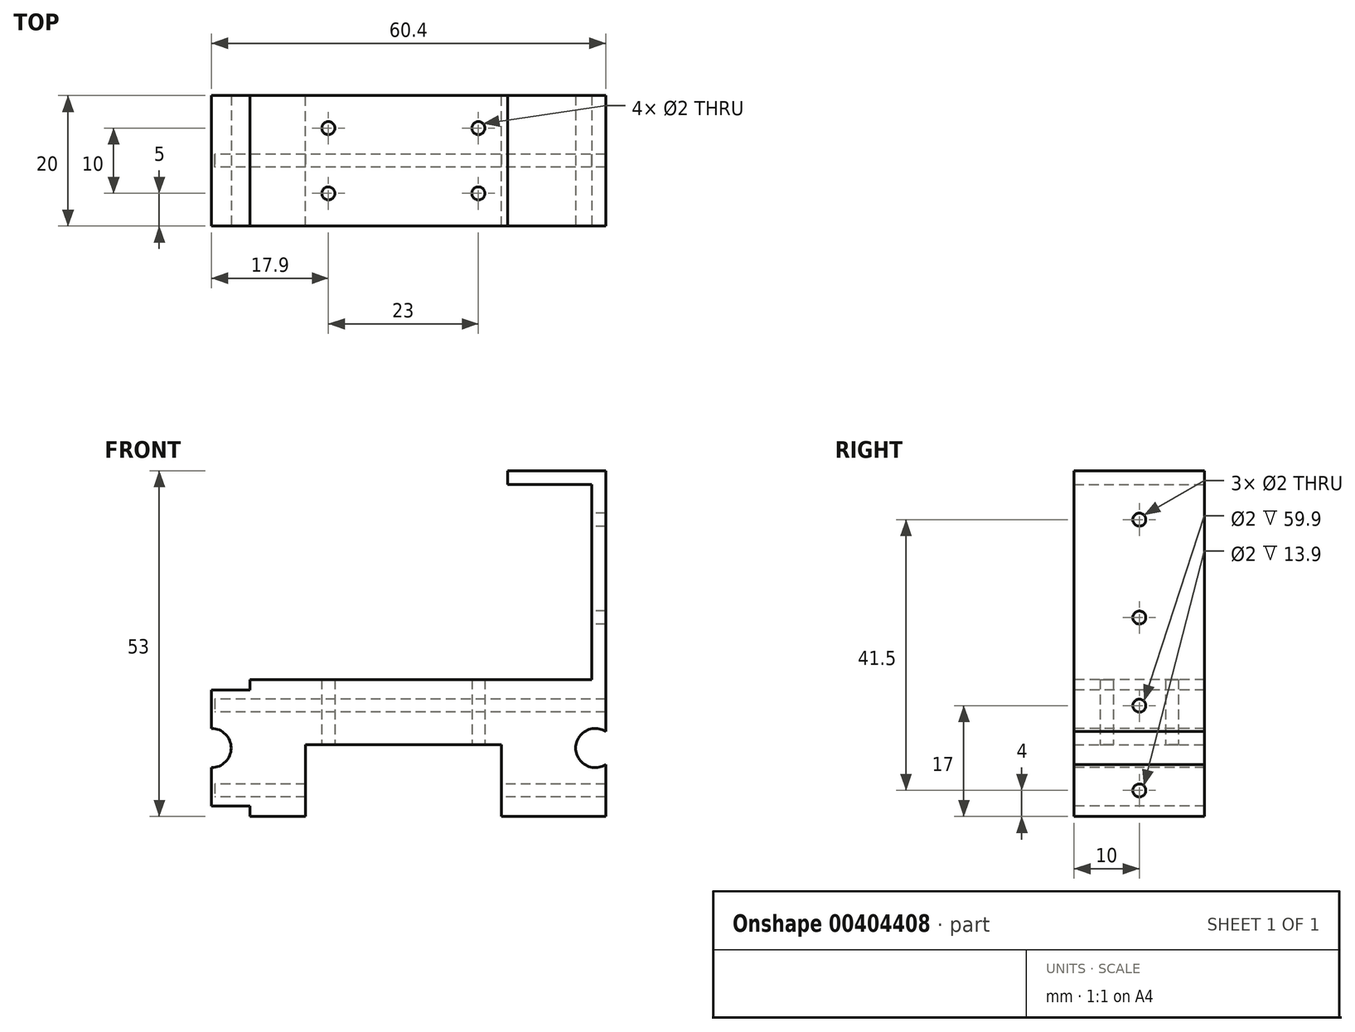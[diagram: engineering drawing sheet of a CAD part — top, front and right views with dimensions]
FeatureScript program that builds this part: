
annotation { "Feature Type Name" : "Feature", "Feature Type Description" : "" }
export const myFeature = defineFeature(function(context is Context, id is Id, definition is map)
    precondition{}
    {
        {
            var Q0;
            Q0=qCreatedBy(makeId("Front.planeOp"),FACE);
            var sketch = newSketch(context, id + "F0", { "sketchPlane" : qUnion([Q0])});
            skLineSegment(sketch, "E0.bottom", {"start": v(31, 26.5) * mm, "end": v(-31, 26.5) * mm});
            skLineSegment(sketch, "E0.top", {"start": v(31, -26.5) * mm, "end": v(-31, -26.5) * mm});
            skLineSegment(sketch, "E0.left", {"start": v(31, 26.5) * mm, "end": v(31, -26.5) * mm});
            skLineSegment(sketch, "E0.right", {"start": v(-31, 26.5) * mm, "end": v(-31, -26.5) * mm});
            skPoint(sketch, "E0.middle", {"position": v(0, 0) * mm});
            skSolve(sketch);
        }
        {
            var Q0;
            Q0=makeQuery(id+"F0.imprint","IMPRINT",FACE,{"disambiguationData":[TD([[makeQuery(id+"F0.imprint","IMPRINT",EDGE,{"derivedFrom":sQuery(id+"F0.wireOp",EDGE,"E0.bottom")}),1.0]])]});
            extrude(context, id + "F1", {"entities" : qUnion([Q0]), "endBound" : BoundingType.SYMMETRIC, "depth" : 20 * mm});
        }
        {
            var Q0;
            Q0=makeQuery(id+"F1.opExtrude","CAP_FACE",FACE,{"disambiguationData":[OSD([sQuery(id+"F0.wireOp",EDGE,"E0.bottom"),sQuery(id+"F0.wireOp",EDGE,"E0.top"),sQuery(id+"F0.wireOp",EDGE,"E0.left"),sQuery(id+"F0.wireOp",EDGE,"E0.right")])],"isStart":false});
            var sketch = newSketch(context, id + "F2", { "sketchPlane" : qUnion([Q0])});
            skLineSegment(sketch, "E1", {"start": v(-31, 26.5) * mm, "end": v(-31, -5.5) * mm});
            skLineSegment(sketch, "E2", {"start": v(-31, -5.5) * mm, "end": v(-28.9, -5.5) * mm});
            skLineSegment(sketch, "E3", {"start": v(-28.9, -5.5) * mm, "end": v(-28.9, 24.4) * mm});
            skLineSegment(sketch, "E4", {"start": v(-28.9, 24.4) * mm, "end": v(-16, 24.4) * mm});
            skLineSegment(sketch, "E5", {"start": v(-16, 24.4) * mm, "end": v(-16, 26.5) * mm});
            skLineSegment(sketch, "E6", {"start": v(-16, 26.5) * mm, "end": v(-31, 26.5) * mm});
            skLineSegment(sketch, "E7", {"start": v(-23.5, -26.5) * mm, "end": v(-31, -26.5) * mm});
            skLineSegment(sketch, "E8", {"start": v(-31, -26.5) * mm, "end": v(-31, -5.5) * mm});
            skLineSegment(sketch, "E9", {"start": v(-31, -5.5) * mm, "end": v(-23.5, -5.5) * mm});
            skLineSegment(sketch, "E10", {"start": v(-23.5, -5.5) * mm, "end": v(-23.5, -7.1) * mm});
            skLineSegment(sketch, "E11", {"start": v(-23.5, -7.1) * mm, "end": v(-29.4, -7.1) * mm});
            skLineSegment(sketch, "E12", {"start": v(-29.4, -7.1) * mm, "end": v(-29.4, -24.9) * mm});
            skLineSegment(sketch, "E13", {"start": v(-29.4, -24.9) * mm, "end": v(-23.5, -24.9) * mm});
            skLineSegment(sketch, "E14", {"start": v(-23.5, -24.9) * mm, "end": v(-23.5, -26.5) * mm});
            skSolve(sketch);
        }
        {
            var Q0;
            {var subQ1=sQuery(id+"F2.wireOp",EDGE,"E1");Q0=makeQuery(id+"F2.imprint","IMPRINT",FACE,{"disambiguationData":[TD([[makeQuery(id+"F2.imprint","IMPRINT",EDGE,{"derivedFrom":subQ1}),1.0]])]});}
            var Q1;
            Q1=makeQuery(id+"F2.imprint","IMPRINT",FACE,{"disambiguationData":[TD([[makeQuery(id+"F2.imprint","IMPRINT",EDGE,{"derivedFrom":sQuery(id+"F2.wireOp",EDGE,"E7")}),-1.0]])]});
            extrude(context, id + "F3", {"entities" : qUnion([Q0, Q1]), "operationType" : NewBodyOperationType.REMOVE, "endBound" : BoundingType.UP_TO_NEXT, "oppositeDirection" : true, "depth" : 25 * mm});
        }
        {
            var Q0;
            Q0=makeQuery(id+"F3.boolean.opBoolean","COPY",FACE,{"derivedFrom":makeQuery(id+"F3.opExtrude","SWEPT_FACE",FACE,{"disambiguationData":[OSD([sQuery(id+"F2.wireOp",EDGE,"E3")])]})});
            var sketch = newSketch(context, id + "F4", { "sketchPlane" : qUnion([Q0])});
            skPoint(sketch, "E15", {"position": v(0, 19) * mm});
            skPoint(sketch, "E16", {"position": v(0, -9.5) * mm});
            skPoint(sketch, "E17", {"position": v(0, -22.5) * mm});
            skPoint(sketch, "E18", {"position": v(0, 4) * mm});
            skSolve(sketch);
        }
        {
            var Q0;
            Q0=sQuery(id+"F4.wireOp",VERTEX,"E15");
            var Q1;
            Q1=sQuery(id+"F4.wireOp",VERTEX,"E18");
            var Q2;
            Q2=sQuery(id+"F4.wireOp",VERTEX,"E16");
            var Q3;
            Q3=sQuery(id+"F4.wireOp",VERTEX,"E17");
            var Q4;
            Q4=makeQuery(id+"F1.opExtrude","SWEPT_BODY",BODY,{"disambiguationData":[OSD([sQuery(id+"F0.wireOp",EDGE,"E0.bottom"),sQuery(id+"F0.wireOp",EDGE,"E0.top"),sQuery(id+"F0.wireOp",EDGE,"E0.left"),sQuery(id+"F0.wireOp",EDGE,"E0.right")])]});
            hole(context, id + "F5", {"style" : HoleStyle.SIMPLE, "endStyle" : HoleEndStyle.THROUGH, "holeDiameter" : 2 * mm, "locations" : qUnion([Q0, Q1, Q2, Q3]), "scope" : qUnion([Q4]), "tappedDepth" : 12 * mm, "tapClearance" : 3});
        }
        {
            var Q0;
            Q0=makeQuery(id+"F1.opExtrude","CAP_FACE",FACE,{"disambiguationData":[OSD([sQuery(id+"F0.wireOp",EDGE,"E0.bottom"),sQuery(id+"F0.wireOp",EDGE,"E0.top"),sQuery(id+"F0.wireOp",EDGE,"E0.left"),sQuery(id+"F0.wireOp",EDGE,"E0.right")])],"isStart":false});
            var sketch = newSketch(context, id + "F6", { "sketchPlane" : qUnion([Q0])});
            skLineSegment(sketch, "E19.bottom", {"start": v(-7, 26.5) * mm, "end": v(2, 26.5) * mm});
            skLineSegment(sketch, "E19.top", {"start": v(-7, 22.25) * mm, "end": v(2, 22.25) * mm});
            skLineSegment(sketch, "E19.left", {"start": v(-7, 26.5) * mm, "end": v(-7, 22.25) * mm});
            skLineSegment(sketch, "E19.right", {"start": v(2, 26.5) * mm, "end": v(2, 22.25) * mm});
            skLineSegment(sketch, "E20.bottom", {"start": v(-7, 22.25) * mm, "end": v(-16, 22.25) * mm});
            skLineSegment(sketch, "E20.top", {"start": v(-7, 26.5) * mm, "end": v(-16, 26.5) * mm});
            skLineSegment(sketch, "E20.left", {"start": v(-7, 22.25) * mm, "end": v(-7, 26.5) * mm});
            skLineSegment(sketch, "E20.right", {"start": v(-16, 22.25) * mm, "end": v(-16, 26.5) * mm});
            skLineSegment(sketch, "E21.bottom", {"start": v(2, 22.25) * mm, "end": v(11, 22.25) * mm});
            skLineSegment(sketch, "E21.top", {"start": v(2, 26.5) * mm, "end": v(11, 26.5) * mm});
            skLineSegment(sketch, "E21.left", {"start": v(2, 22.25) * mm, "end": v(2, 26.5) * mm});
            skLineSegment(sketch, "E21.right", {"start": v(11, 22.25) * mm, "end": v(11, 26.5) * mm});
            skLineSegment(sketch, "E22.bottom", {"start": v(11, 22.25) * mm, "end": v(16, 22.25) * mm});
            skLineSegment(sketch, "E22.top", {"start": v(11, 26.5) * mm, "end": v(16, 26.5) * mm});
            skLineSegment(sketch, "E22.right", {"start": v(16, 22.25) * mm, "end": v(16, 26.5) * mm});
            skSolve(sketch);
        }
        {
            var Q0;
            Q0=makeQuery(id+"F6.imprint","IMPRINT",FACE,{"disambiguationData":[TD([[makeQuery(id+"F6.imprint","IMPRINT",EDGE,{"derivedFrom":sQuery(id+"F6.wireOp",EDGE,"E19.bottom")}),1.0]])]});
            var Q1;
            {var subQ2=sQuery(id+"F6.wireOp",EDGE,"E20.bottom");Q1=makeQuery(id+"F6.imprint","IMPRINT",FACE,{"disambiguationData":[TD([[makeQuery(id+"F6.imprint","IMPRINT",EDGE,{"derivedFrom":subQ2}),-1.0]])]});}
            var Q2;
            Q2=makeQuery(id+"F6.imprint","IMPRINT",FACE,{"disambiguationData":[TD([[makeQuery(id+"F6.imprint","IMPRINT",EDGE,{"derivedFrom":sQuery(id+"F6.wireOp",EDGE,"E21.bottom")}),1.0]])]});
            var Q3;
            {var subQ2=sQuery(id+"F6.wireOp",EDGE,"E22.bottom");Q3=makeQuery(id+"F6.imprint","IMPRINT",FACE,{"disambiguationData":[TD([[makeQuery(id+"F6.imprint","IMPRINT",EDGE,{"derivedFrom":subQ2}),1.0]])]});}
            extrude(context, id + "F7", {"entities" : qUnion([Q0, Q1, Q2, Q3]), "operationType" : NewBodyOperationType.REMOVE, "endBound" : BoundingType.UP_TO_NEXT, "oppositeDirection" : true, "depth" : 25 * mm});
        }
        {
            var Q0;
            Q0=makeQuery(id+"F1.opExtrude","CAP_FACE",FACE,{"disambiguationData":[OSD([sQuery(id+"F0.wireOp",EDGE,"E0.bottom"),sQuery(id+"F0.wireOp",EDGE,"E0.top"),sQuery(id+"F0.wireOp",EDGE,"E0.left"),sQuery(id+"F0.wireOp",EDGE,"E0.right")])],"isStart":false});
            var sketch = newSketch(context, id + "F8", { "sketchPlane" : qUnion([Q0])});
            skLineSegment(sketch, "E23.bottom", {"start": v(-28.9, -5.5) * mm, "end": v(28.9, -5.5) * mm});
            skLineSegment(sketch, "E23.top", {"start": v(-28.9, 24.4) * mm, "end": v(28.9, 24.4) * mm});
            skLineSegment(sketch, "E23.left", {"start": v(-28.9, -5.5) * mm, "end": v(-28.9, 24.4) * mm});
            skLineSegment(sketch, "E23.right", {"start": v(28.9, -5.5) * mm, "end": v(28.9, 24.4) * mm});
            skSolve(sketch);
        }
        {
            var Q0;
            Q0 = qSketchRegion(id + "F8", true);
            extrude(context, id + "F9", {"entities" : qUnion([Q0]), "operationType" : NewBodyOperationType.REMOVE, "oppositeDirection" : true, "depth" : 25 * mm});
        }
        {
            var Q0;
            Q0=makeQuery(id+"F1.opExtrude","SWEPT_FACE",FACE,{"disambiguationData":[OSD([sQuery(id+"F0.wireOp",EDGE,"E0.top")])]});
            var sketch = newSketch(context, id + "F10", { "sketchPlane" : qUnion([Q0])});
            skLineSegment(sketch, "E24.bottom", {"start": v(-15, 10) * mm, "end": v(15, 10) * mm});
            skLineSegment(sketch, "E24.top", {"start": v(-15, -10) * mm, "end": v(15, -10) * mm});
            skLineSegment(sketch, "E24.left", {"start": v(-15, 10) * mm, "end": v(-15, -10) * mm});
            skLineSegment(sketch, "E24.right", {"start": v(15, 10) * mm, "end": v(15, -10) * mm});
            skPoint(sketch, "E24.middle", {"position": v(0, 0) * mm});
            skSolve(sketch);
        }
        {
            var Q0;
            Q0 = qSketchRegion(id + "F10", true);
            extrude(context, id + "F11", {"entities" : qUnion([Q0]), "operationType" : NewBodyOperationType.REMOVE, "oppositeDirection" : true, "depth" : 11 * mm});
        }
        {
            var Q0;
            Q0=makeQuery(id+"F11.boolean.opBoolean","COPY",FACE,{"derivedFrom":makeQuery(id+"F11.opExtrude","CAP_FACE",FACE,{"disambiguationData":[OSD([sQuery(id+"F10.wireOp",EDGE,"E24.bottom"),sQuery(id+"F10.wireOp",EDGE,"E24.top"),sQuery(id+"F10.wireOp",EDGE,"E24.left"),sQuery(id+"F10.wireOp",EDGE,"E24.right")])],"isStart":false})});
            var sketch = newSketch(context, id + "F12", { "sketchPlane" : qUnion([Q0])});
            skLineSegment(sketch, "E25.bottom", {"start": v(-11.5, 5) * mm, "end": v(11.5, 5) * mm});
            skLineSegment(sketch, "E25.top", {"start": v(-11.5, -5) * mm, "end": v(11.5, -5) * mm});
            skLineSegment(sketch, "E25.left", {"start": v(-11.5, 5) * mm, "end": v(-11.5, -5) * mm});
            skLineSegment(sketch, "E25.right", {"start": v(11.5, 5) * mm, "end": v(11.5, -5) * mm});
            skPoint(sketch, "E25.middle", {"position": v(0, 0) * mm});
            skSolve(sketch);
        }
        {
            var Q0;
            Q0=sQuery(id+"F12.wireOp",VERTEX,"E25.bottom.start");
            var Q1;
            Q1=sQuery(id+"F12.wireOp",VERTEX,"E25.right.start");
            var Q2;
            Q2=sQuery(id+"F12.wireOp",VERTEX,"E25.right.end");
            var Q3;
            Q3=sQuery(id+"F12.wireOp",VERTEX,"E25.left.end");
            var Q4;
            Q4=makeQuery(id+"F1.opExtrude","SWEPT_BODY",BODY,{"disambiguationData":[OSD([sQuery(id+"F0.wireOp",EDGE,"E0.bottom"),sQuery(id+"F0.wireOp",EDGE,"E0.top"),sQuery(id+"F0.wireOp",EDGE,"E0.left"),sQuery(id+"F0.wireOp",EDGE,"E0.right")])]});
            hole(context, id + "F13", {"style" : HoleStyle.SIMPLE, "endStyle" : HoleEndStyle.BLIND, "holeDiameter" : 2 * mm, "holeDepth" : 80 * mm, "isTappedThrough" : true, "tappedDepth" : 12 * mm, "tapClearance" : 3, "locations" : qUnion([Q0, Q1, Q2, Q3]), "scope" : qUnion([Q4])});
        }
        {
            var Q0;
            Q0=makeQuery(id+"F1.opExtrude","CAP_FACE",FACE,{"disambiguationData":[OSD([sQuery(id+"F0.wireOp",EDGE,"E0.bottom"),sQuery(id+"F0.wireOp",EDGE,"E0.top"),sQuery(id+"F0.wireOp",EDGE,"E0.left"),sQuery(id+"F0.wireOp",EDGE,"E0.right")])],"isStart":false});
            var sketch = newSketch(context, id + "F14", { "sketchPlane" : qUnion([Q0])});
            skCircle(sketch, "E26", {"center": v(-29.4, -16) * mm, "radius": 3 * mm});
            skCircle(sketch, "E27", {"center": v(29.4, -16) * mm, "radius": 3 * mm});
            skSolve(sketch);
        }
        {
            var Q0;
            Q0 = qSketchRegion(id + "F14", true);
            extrude(context, id + "F15", {"entities" : qUnion([Q0]), "operationType" : NewBodyOperationType.REMOVE, "oppositeDirection" : true, "depth" : 25 * mm});
        }
    });
